# Revit family: Faucet-Two_Handle-American_Standard-Heritage-7295252.002
name_source: partatom
category: Plumbing Fixtures
units: mm (PartAtom-declared; Revit-internal decimal feet)

## family parameters
Cut with Voids When Loaded = No
Host = Face
OmniClass Number = 23.45.55.17
OmniClass Title = Mixing Faucets
Part Type = Normal
Room Calculation Point = No
Round Connector Dimension = Use Diameter
Shared = Yes

## types (1)
- 7295252.002
    ADA Compliant = Yes
    Assembly Code = D2020300
    CW Connection = Yes
    CWFU = 1.5
    Cold Water Connection Diameter = 1/2"
    Default Elevation = 34"
    Description = Heritage® 2-Handle Wall Mount Kitchen Faucet 2.2 gpm/8.3 L/min With Soap Dish
    Finish = Metal-American Standard-002-Polished Chrome
    HW Connection = Yes
    HWFU = 1.5
    Hot Water Connection Diameter = 1/2"
    Installation Type = Wall Mounted
    Length = 7 7/8"
    Manufacturer = American Standard
    Material = Metal-American Standard-002-Polished Chrome
    Model = 7295252.002
    Product Documentation Link = https://americanstandard.box.com
    Product Page URL = https://www.americanstandard-us.com
    URL = http://www.americanstandard-us.com
    Vent Connection = No
    WFU = 2
    Warranty Information = Limited Lifetime Warranty
    Waste Connection = No

## geometry (parser evidence)
native form markers: Sweep x2
no freeform markers — native parametric forms only
